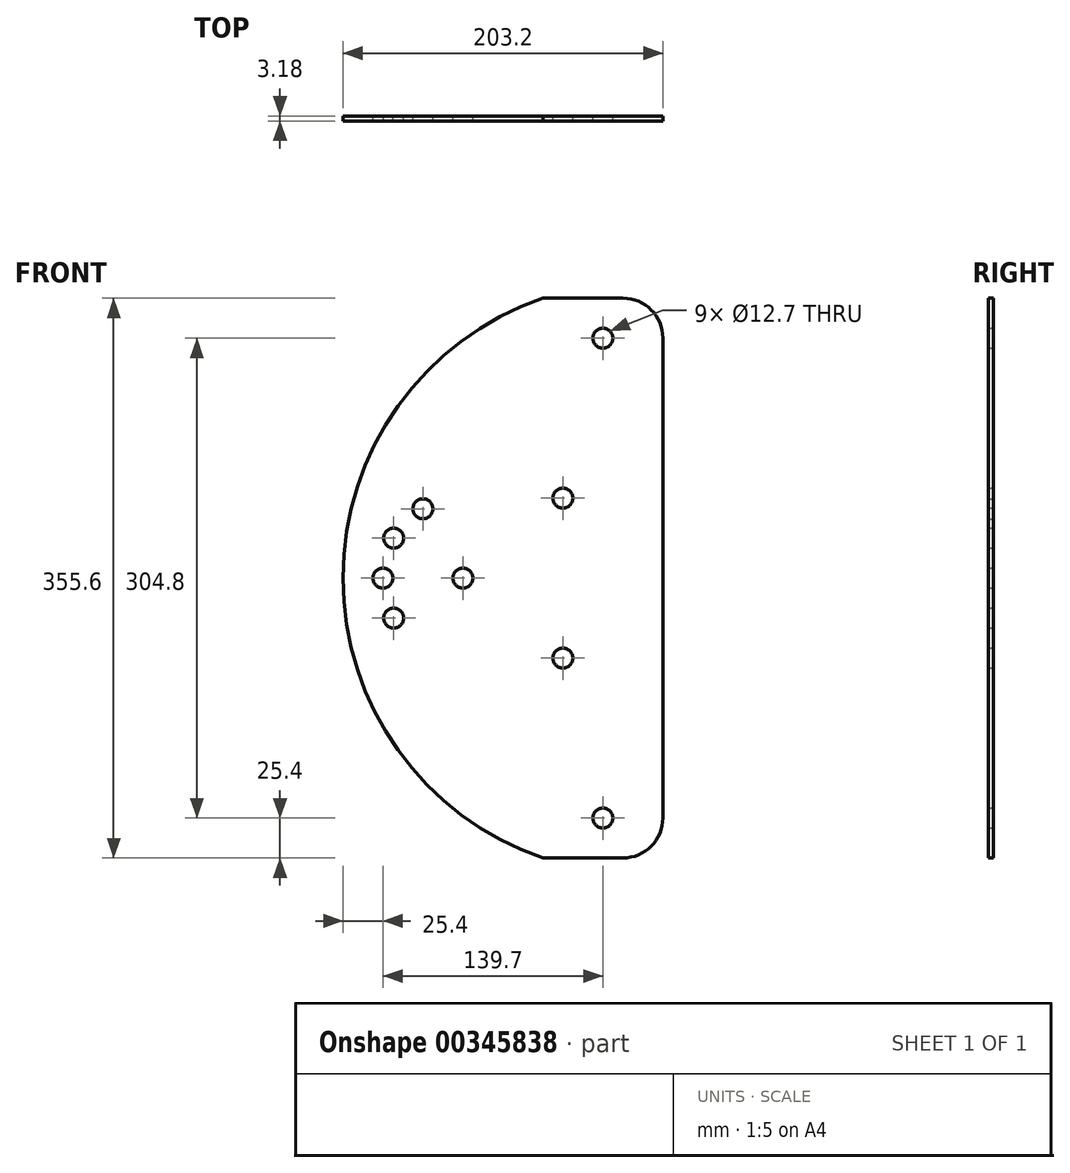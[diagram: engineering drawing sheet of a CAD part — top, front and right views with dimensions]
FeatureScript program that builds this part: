
annotation { "Feature Type Name" : "Feature", "Feature Type Description" : "" }
export const myFeature = defineFeature(function(context is Context, id is Id, definition is map)
    precondition{}
    {
        {
            var Q0;
            Q0=qCreatedBy(makeId("Front.planeOp"),FACE);
            var sketch = newSketch(context, id + "F1", { "sketchPlane" : qUnion([Q0])});
            skLineSegment(sketch, "E0.bottom", {"start": v(-38.1, -177.8) * mm, "end": v(12.7, -177.8) * mm});
            skLineSegment(sketch, "E0.top", {"start": v(-38.1, 177.8) * mm, "end": v(12.7, 177.8) * mm});
            skLineSegment(sketch, "E0.left", {"start": v(-38.1, -177.8) * mm, "end": v(-38.1, 177.8) * mm});
            skLineSegment(sketch, "E0.right", {"start": v(38.1, -152.4) * mm, "end": v(38.1, 152.4) * mm});
            skPoint(sketch, "E0.middle", {"position": v(0, 0) * mm});
            skArc(sketch, "E1", {"start": v(-38.1, 177.8) * mm, "mid": v(-165.1, 0) * mm, "end": v(-38.1, -177.8) * mm});
            skPoint(sketch, "E2", {"position": v(-139.7, 0) * mm});
            skPoint(sketch, "E3", {"position": v(-88.9, 0) * mm});
            skPoint(sketch, "E4.visualSharp", {"position": v(38.1, 177.8) * mm});
            skArc(sketch, "E4.filletArc", {"start": v(38.1, 152.4) * mm, "mid": v(30.66, 170.36) * mm, "end": v(12.7, 177.8) * mm});
            skPoint(sketch, "E5.visualSharp", {"position": v(38.1, -177.8) * mm});
            skArc(sketch, "E5.filletArc", {"start": v(12.7, -177.8) * mm, "mid": v(30.66, -170.36) * mm, "end": v(38.1, -152.4) * mm});
            skPoint(sketch, "E6", {"position": v(0, 152.4) * mm});
            skPoint(sketch, "E7", {"position": v(0, -152.4) * mm});
            skPoint(sketch, "E8", {"position": v(0, -50.8) * mm});
            skPoint(sketch, "E9", {"position": v(0, 50.8) * mm});
            skPoint(sketch, "E10", {"position": v(-132.9, 25.4) * mm});
            skPoint(sketch, "E11", {"position": v(-132.9, -25.4) * mm});
            skPoint(sketch, "E12", {"position": v(-114.3, 44) * mm});
            skPoint(sketch, "E13", {"position": v(-25.4, -50.8) * mm});
            skPoint(sketch, "E14", {"position": v(-25.4, 50.8) * mm});
            skSolve(sketch);
        }
        {
            var Q0;
            Q0=makeQuery(id+"F1.imprint","IMPRINT",FACE,{"disambiguationData":[TD([[makeQuery(id+"F1.imprint","IMPRINT",EDGE,{"derivedFrom":sQuery(id+"F1.wireOp",EDGE,"E0.left")}),1.0]])]});
            var Q1;
            Q1=makeQuery(id+"F1.imprint","IMPRINT",FACE,{"disambiguationData":[TD([[makeQuery(id+"F1.imprint","IMPRINT",EDGE,{"derivedFrom":sQuery(id+"F1.wireOp",EDGE,"E0.bottom")}),1.0]])]});
            extrude(context, id + "F0", {"entities" : qUnion([Q0, Q1]), "depth" : 3.17 * mm});
        }
        {
            var Q0;
            Q0=sQuery(id+"F1.wireOp",VERTEX,"E3");
            var Q1;
            Q1=sQuery(id+"F1.wireOp",VERTEX,"E2");
            var Q2;
            Q2=sQuery(id+"F1.wireOp",VERTEX,"E7");
            var Q3;
            Q3=sQuery(id+"F1.wireOp",VERTEX,"E6");
            var Q4;
            Q4=sQuery(id+"F1.wireOp",VERTEX,"E11");
            var Q5;
            Q5=sQuery(id+"F1.wireOp",VERTEX,"E10");
            var Q6;
            Q6=sQuery(id+"F1.wireOp",VERTEX,"E12");
            var Q7;
            Q7=sQuery(id+"F1.wireOp",VERTEX,"E14");
            var Q8;
            Q8=sQuery(id+"F1.wireOp",VERTEX,"E13");
            var Q9;
            Q9=makeQuery(id+"F0.opExtrude","SWEPT_BODY",BODY,{"disambiguationData":[OSD([sQuery(id+"F1.wireOp",EDGE,"E0.bottom"),sQuery(id+"F1.wireOp",EDGE,"E0.top"),sQuery(id+"F1.wireOp",EDGE,"E0.right"),sQuery(id+"F1.wireOp",EDGE,"E1")])]});
            var Q10;
            Q10=makeQuery(id+"F0.opExtrude","SWEPT_BODY",BODY,{"disambiguationData":[OSD([sQuery(id+"F1.wireOp",EDGE,"E0.bottom"),sQuery(id+"F1.wireOp",EDGE,"E0.top"),sQuery(id+"F1.wireOp",EDGE,"E0.right"),sQuery(id+"F1.wireOp",EDGE,"E1")])]});
            hole(context, id + "F2", {"style" : HoleStyle.SIMPLE, "endStyle" : HoleEndStyle.THROUGH, "oppositeDirection" : true, "holeDiameter" : 12.7 * mm, "locations" : qUnion([Q0, Q1, Q2, Q3, Q4, Q5, Q6, Q7, Q8]), "scope" : qUnion([Q9, Q10]), "isTappedThrough" : true});
        }
    });
